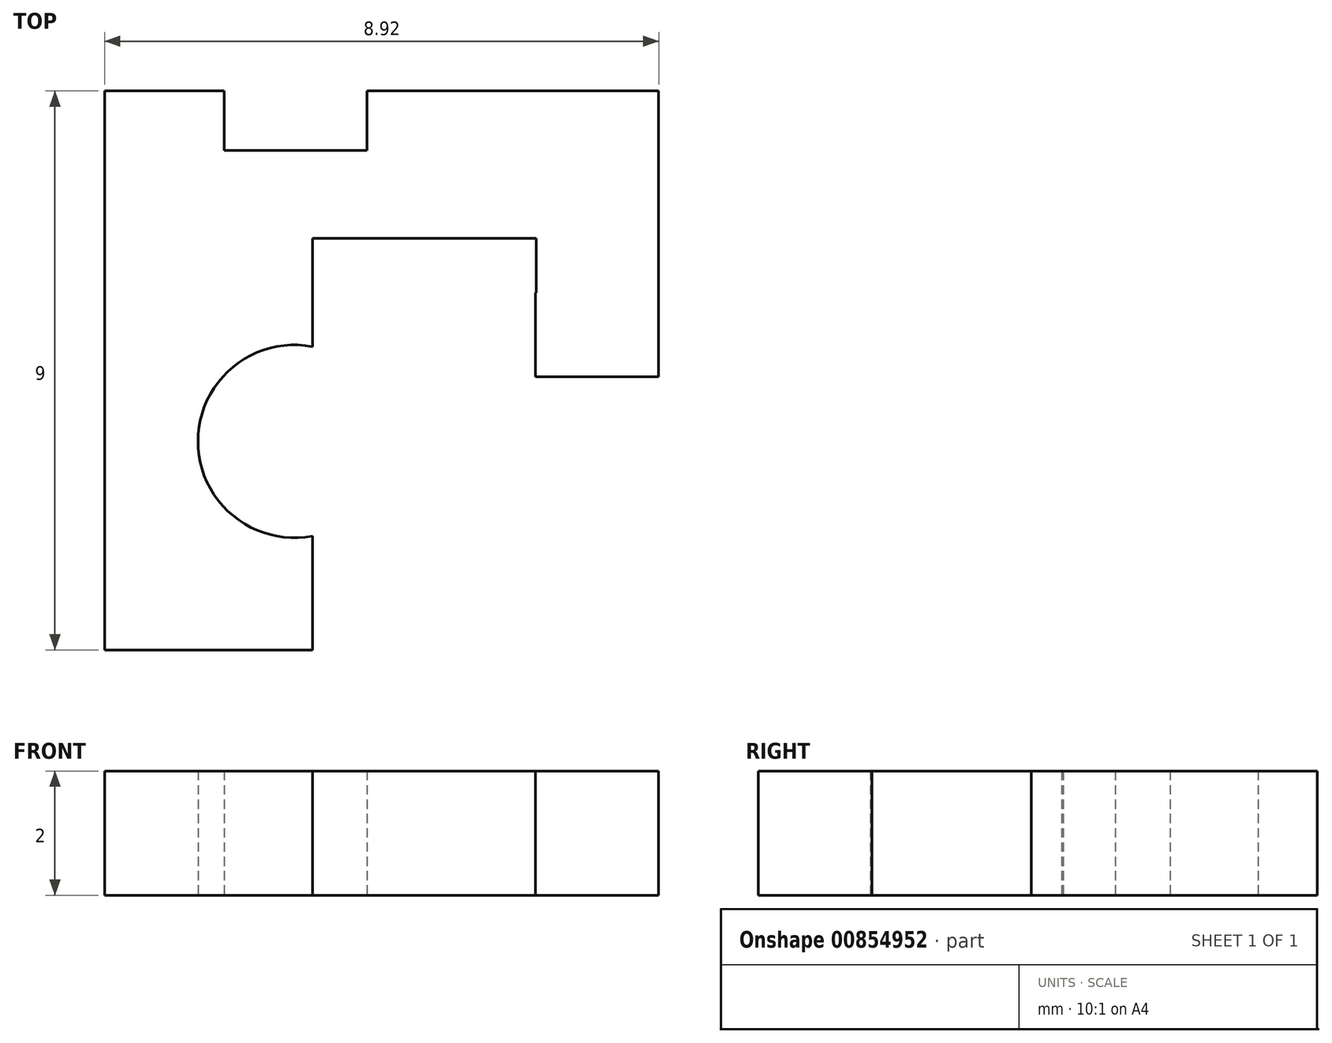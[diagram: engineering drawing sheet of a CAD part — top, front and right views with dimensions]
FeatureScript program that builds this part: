
annotation { "Feature Type Name" : "Feature", "Feature Type Description" : "" }
export const myFeature = defineFeature(function(context is Context, id is Id, definition is map)
    precondition{}
    {
        {
            var Q0;
            Q0=qCreatedBy(makeId("Top.planeOp"),FACE);
            var sketch = newSketch(context, id + "F0", { "sketchPlane" : qUnion([Q0])});
            skLineSegment(sketch, "E0", {"start": v(0, 0) * mm, "end": v(0, 9) * mm});
            skLineSegment(sketch, "E1", {"start": v(0, 9) * mm, "end": v(1.92, 9) * mm});
            skLineSegment(sketch, "E2", {"start": v(1.92, 9) * mm, "end": v(1.92, 8.04) * mm});
            skLineSegment(sketch, "E3", {"start": v(1.92, 8.04) * mm, "end": v(4.22, 8.04) * mm});
            skLineSegment(sketch, "E4", {"start": v(4.22, 8.04) * mm, "end": v(4.22, 9) * mm});
            skLineSegment(sketch, "E5", {"start": v(4.22, 9) * mm, "end": v(8.92, 9) * mm});
            skLineSegment(sketch, "E6", {"start": v(8.92, 9) * mm, "end": v(8.92, 4.4) * mm});
            skLineSegment(sketch, "E7", {"start": v(8.92, 4.4) * mm, "end": v(6.93, 4.4) * mm});
            skLineSegment(sketch, "E8", {"start": v(6.93, 4.4) * mm, "end": v(6.93, 5.75) * mm});
            skLineSegment(sketch, "E9", {"start": v(6.93, 5.75) * mm, "end": v(6.95, 5.75) * mm});
            skLineSegment(sketch, "E10", {"start": v(6.95, 5.75) * mm, "end": v(6.95, 6.63) * mm});
            skLineSegment(sketch, "E11", {"start": v(6.95, 6.63) * mm, "end": v(3.34, 6.63) * mm});
            skLineSegment(sketch, "E12", {"start": v(3.34, 6.63) * mm, "end": v(3.34, 4.88) * mm});
            skArc(sketch, "E13", {"start": v(3.34, 4.88) * mm, "mid": v(1.5, 3.36) * mm, "end": v(3.34, 1.83) * mm});
            skLineSegment(sketch, "E14", {"start": v(3.34, 1.83) * mm, "end": v(3.34, 0) * mm});
            skLineSegment(sketch, "E15", {"start": v(3.34, 0) * mm, "end": v(0, 0) * mm});
            skSolve(sketch);
        }
        {
            var Q0;
            Q0=makeQuery(id+"F0.imprint","IMPRINT",FACE,{"disambiguationData":[TD([[makeQuery(id+"F0.imprint","IMPRINT",EDGE,{"derivedFrom":sQuery(id+"F0.wireOp",EDGE,"E0")}),-1.0]])]});
            extrude(context, id + "F1", {"entities" : qUnion([Q0]), "depth" : 2 * mm, "offsetDistance" : 25 * mm});
        }
    });
